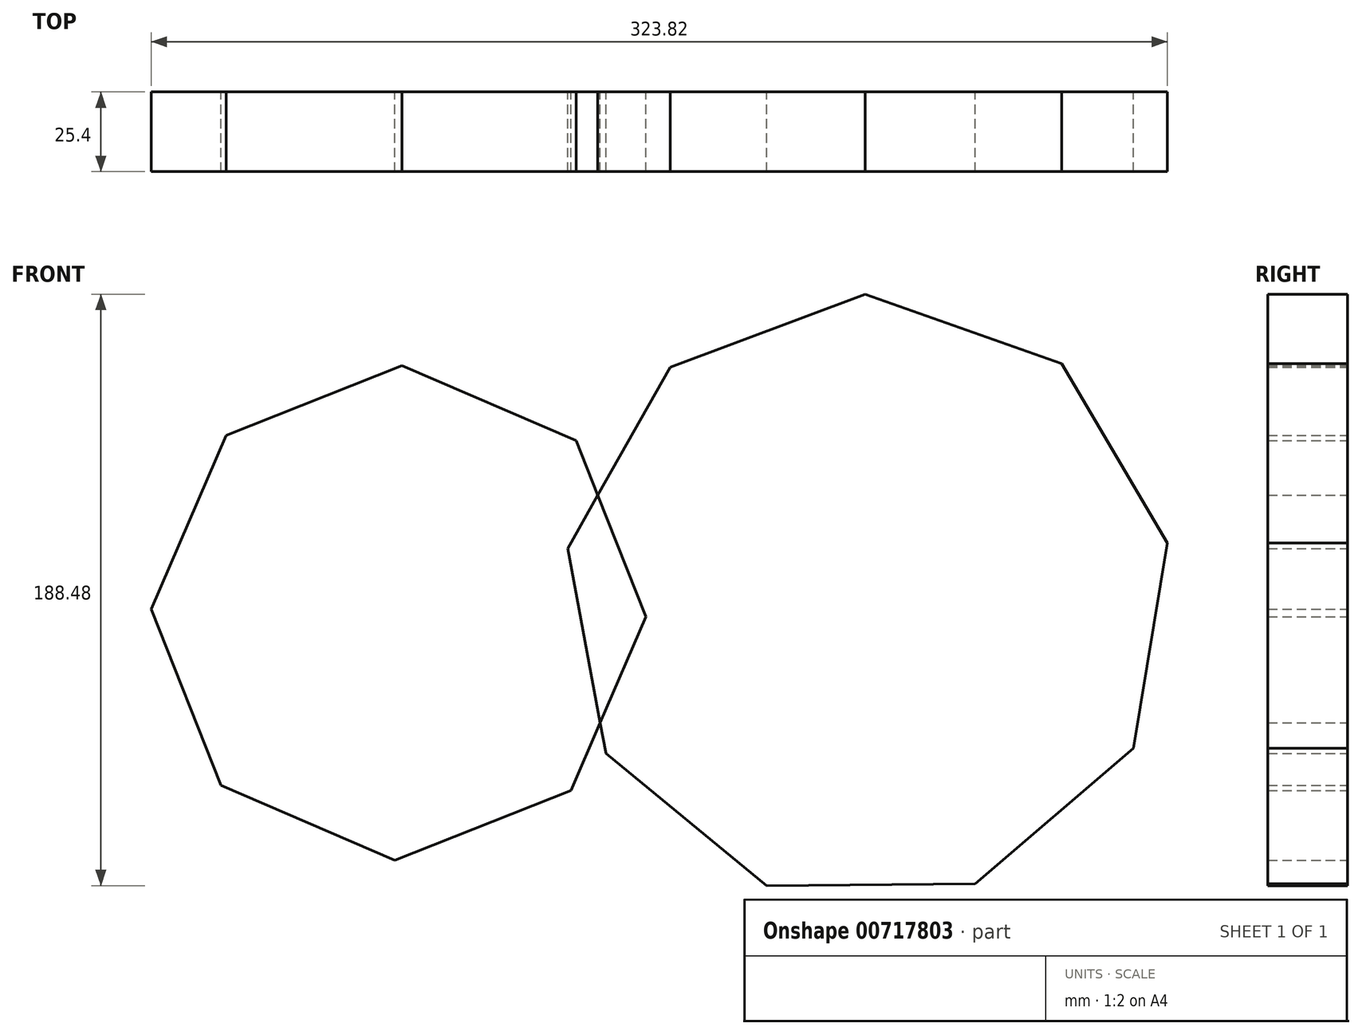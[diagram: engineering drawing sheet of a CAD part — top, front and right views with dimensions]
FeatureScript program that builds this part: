
annotation { "Feature Type Name" : "Feature", "Feature Type Description" : "" }
export const myFeature = defineFeature(function(context is Context, id is Id, definition is map)
    precondition{}
    {
        {
            var Q0;
            Q0=qCreatedBy(makeId("Front.planeOp"),FACE);
            var sketch = newSketch(context, id + "F0", { "sketchPlane" : qUnion([Q0])});
            skCircle(sketch, "E0.cCircle", {"center": v(-18, -39.24) * mm, "radius": 91.16 * mm, "construction": true});
            skLineSegment(sketch, "E0.0", {"start": v(-18.93, 57.77) * mm, "end": v(43.65, 35.67) * mm});
            skLineSegment(sketch, "E0.1", {"start": v(43.65, 35.67) * mm, "end": v(77.37, -21.48) * mm});
            skLineSegment(sketch, "E0.2", {"start": v(77.37, -21.48) * mm, "end": v(66.48, -86.94) * mm});
            skLineSegment(sketch, "E0.3", {"start": v(66.48, -86.94) * mm, "end": v(16.05, -130.08) * mm});
            skLineSegment(sketch, "E0.4", {"start": v(16.05, -130.08) * mm, "end": v(-50.3, -130.71) * mm});
            skLineSegment(sketch, "E0.5", {"start": v(-50.3, -130.71) * mm, "end": v(-101.54, -88.55) * mm});
            skLineSegment(sketch, "E0.6", {"start": v(-101.54, -88.55) * mm, "end": v(-113.7, -23.3) * mm});
            skLineSegment(sketch, "E0.7", {"start": v(-113.7, -23.3) * mm, "end": v(-81.06, 34.48) * mm});
            skLineSegment(sketch, "E0.8", {"start": v(-81.06, 34.48) * mm, "end": v(-18.93, 57.77) * mm});
            skPoint(sketch, "E0.0.midPoint", {"position": v(12.36, 46.72) * mm});
            skCircle(sketch, "E1.cCircle", {"center": v(-167.61, -43.83) * mm, "radius": 72.84 * mm, "construction": true});
            skLineSegment(sketch, "E1.0", {"start": v(-222.54, 12.73) * mm, "end": v(-166.46, 35) * mm});
            skLineSegment(sketch, "E1.1", {"start": v(-166.46, 35) * mm, "end": v(-111.05, 11.1) * mm});
            skLineSegment(sketch, "E1.2", {"start": v(-111.05, 11.1) * mm, "end": v(-88.78, -44.99) * mm});
            skLineSegment(sketch, "E1.3", {"start": v(-88.78, -44.99) * mm, "end": v(-112.69, -100.4) * mm});
            skLineSegment(sketch, "E1.4", {"start": v(-112.69, -100.4) * mm, "end": v(-168.77, -122.67) * mm});
            skLineSegment(sketch, "E1.5", {"start": v(-168.77, -122.67) * mm, "end": v(-224.17, -98.76) * mm});
            skLineSegment(sketch, "E1.6", {"start": v(-224.17, -98.76) * mm, "end": v(-246.45, -42.68) * mm});
            skLineSegment(sketch, "E1.7", {"start": v(-246.45, -42.68) * mm, "end": v(-222.54, 12.73) * mm});
            skPoint(sketch, "E1.0.midPoint", {"position": v(-194.5, 23.86) * mm});
            skSolve(sketch);
        }
        {
            var Q0;
            Q0=makeQuery(id+"F0.imprint","IMPRINT",FACE,{"disambiguationData":[TD([[makeQuery(id+"F0.imprint","IMPRINT",EDGE,{"derivedFrom":sQuery(id+"F0.wireOp",EDGE,"E0.0")}),-1.0]])]});
            var Q1;
            Q1=makeQuery(id+"F0.imprint","IMPRINT",FACE,{"disambiguationData":[TD([[makeQuery(id+"F0.imprint","IMPRINT",EDGE,{"derivedFrom":sQuery(id+"F0.wireOp",EDGE,"E1.0")}),-1.0]])]});
            extrude(context, id + "F1", {"entities" : qUnion([Q0, Q1]), "depth" : 25.4 * mm, "offsetDistance" : 25.4 * mm});
        }
    });
